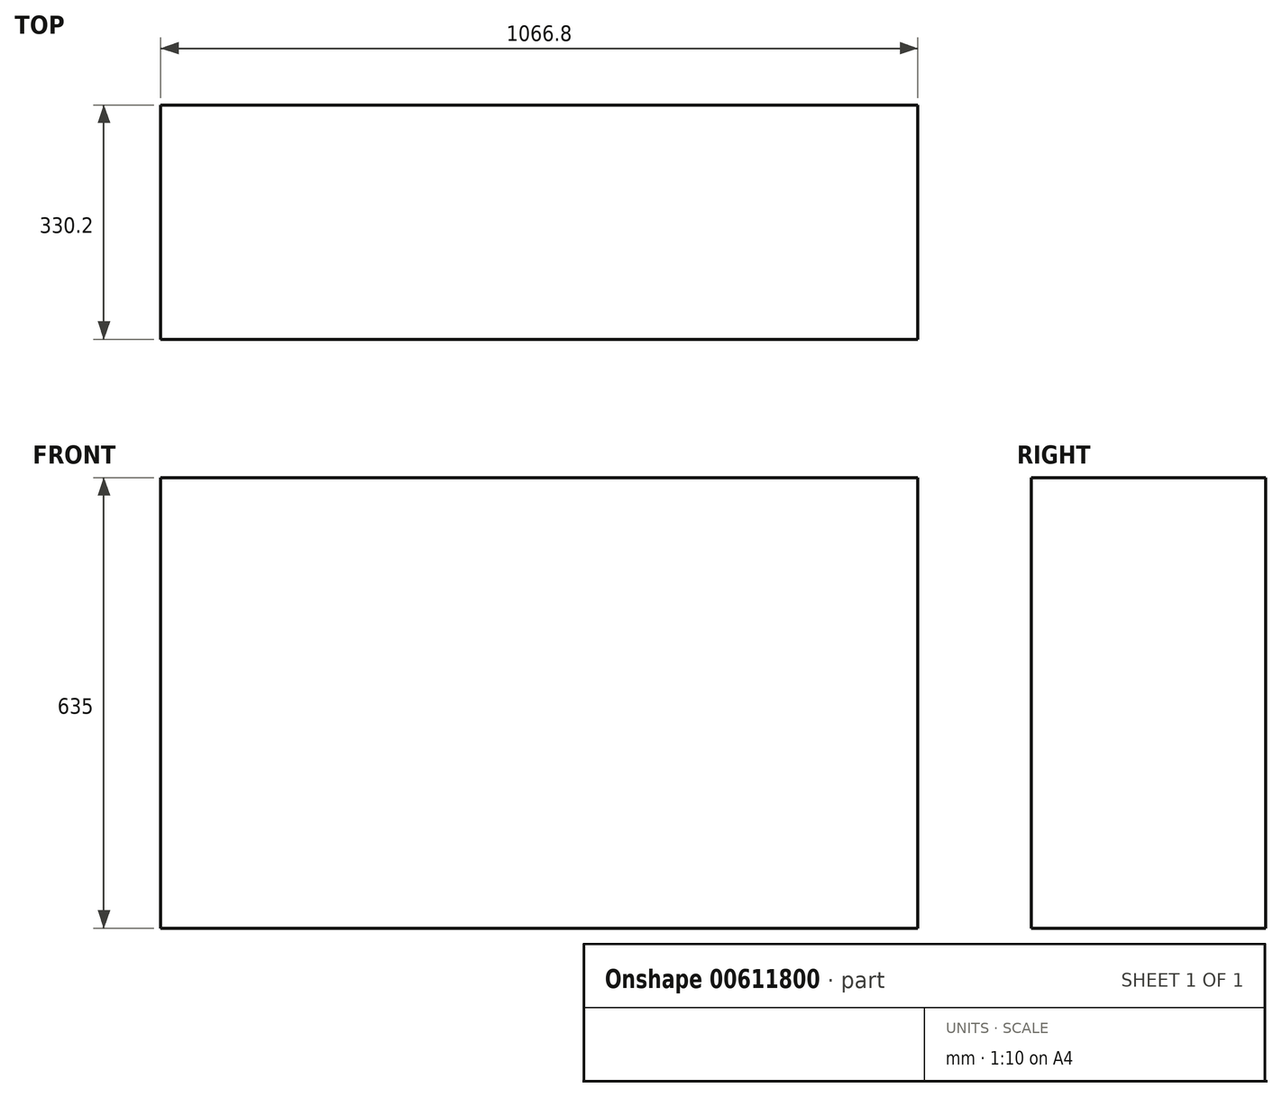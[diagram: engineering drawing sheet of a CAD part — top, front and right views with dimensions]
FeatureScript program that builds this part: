
annotation { "Feature Type Name" : "Feature", "Feature Type Description" : "" }
export const myFeature = defineFeature(function(context is Context, id is Id, definition is map)
    precondition{}
    {
        {
            var Q0;
            Q0=qCreatedBy(makeId("Front.planeOp"),FACE);
            var sketch = newSketch(context, id + "F0", { "sketchPlane" : qUnion([Q0])});
            skLineSegment(sketch, "E0.bottom", {"start": v(-533.4, 635) * mm, "end": v(533.4, 635) * mm});
            skLineSegment(sketch, "E0.top", {"start": v(-533.4, 0) * mm, "end": v(533.4, 0) * mm});
            skLineSegment(sketch, "E0.left", {"start": v(-533.4, 635) * mm, "end": v(-533.4, 0) * mm});
            skLineSegment(sketch, "E0.right", {"start": v(533.4, 635) * mm, "end": v(533.4, 0) * mm});
            skSolve(sketch);
        }
        {
            var Q0;
            Q0 = qSketchRegion(id + "F0", true);
            extrude(context, id + "F1", {"entities" : qUnion([Q0]), "depth" : 330.2 * mm, "offsetDistance" : 25.4 * mm});
        }
    });
